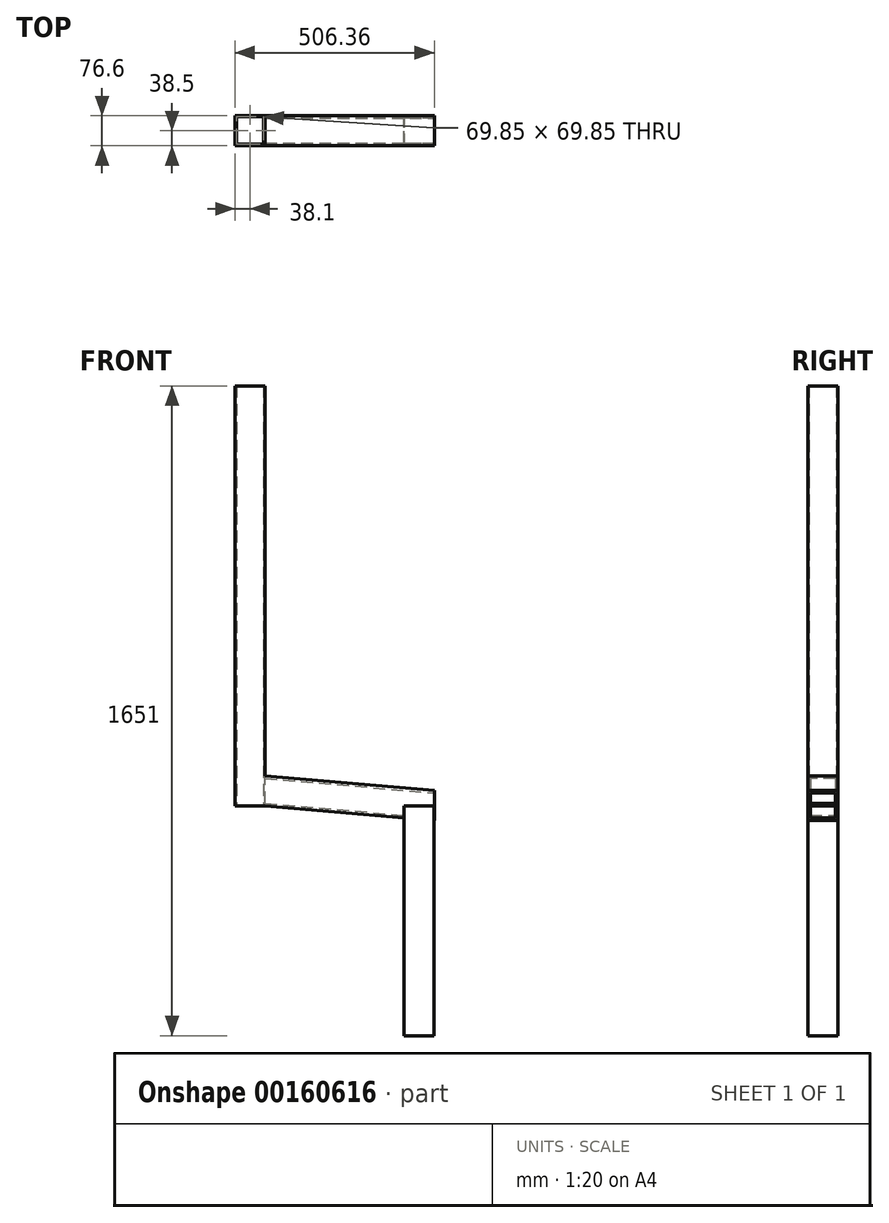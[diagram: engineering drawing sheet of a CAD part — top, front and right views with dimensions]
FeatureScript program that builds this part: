
annotation { "Feature Type Name" : "Feature", "Feature Type Description" : "" }
export const myFeature = defineFeature(function(context is Context, id is Id, definition is map)
    precondition{}
    {
        {
            var Q0;
            Q0=qCreatedBy(makeId("Top.planeOp"),FACE);
            var sketch = newSketch(context, id + "F0", { "sketchPlane" : qUnion([Q0])});
            skLineSegment(sketch, "E0.bottom", {"start": v(-38.1, -38.1) * mm, "end": v(38.1, -38.1) * mm});
            skLineSegment(sketch, "E0.top", {"start": v(-38.1, 38.1) * mm, "end": v(38.1, 38.1) * mm});
            skLineSegment(sketch, "E0.left", {"start": v(-38.1, -38.1) * mm, "end": v(-38.1, 38.1) * mm});
            skLineSegment(sketch, "E0.right", {"start": v(38.1, -38.1) * mm, "end": v(38.1, 38.1) * mm});
            skPoint(sketch, "E0.middle", {"position": v(0, 0) * mm});
            skLineSegment(sketch, "E1.bottom", {"start": v(-34.92, -38.22) * mm, "end": v(34.93, -38.22) * mm});
            skLineSegment(sketch, "E1.top", {"start": v(-34.93, 38.22) * mm, "end": v(34.92, 38.22) * mm});
            skLineSegment(sketch, "E1.left", {"start": v(-34.92, -38.22) * mm, "end": v(-34.93, 38.22) * mm});
            skLineSegment(sketch, "E1.right", {"start": v(34.93, -38.22) * mm, "end": v(34.92, 38.22) * mm});
            skSolve(sketch);
        }
        {
            var Q0;
            Q0=makeQuery(id+"F0.imprint","IMPRINT",FACE,{"disambiguationData":[TD([[makeQuery(id+"F0.imprint","IMPRINT",EDGE,{"derivedFrom":sQuery(id+"F0.wireOp",EDGE,"E0.bottom")}),1.0]])]});
            extrude(context, id + "F1", {"entities" : qUnion([Q0]), "depth" : 1066.8 * mm});
        }
        {
            var Q0;
            Q0=makeQuery(id+"F1.opExtrude","SWEPT_FACE",FACE,{"disambiguationData":[OSD([sQuery(id+"F0.wireOp",EDGE,"E0.right")])]});
            var sketch = newSketch(context, id + "F2", { "sketchPlane" : qUnion([Q0])});
            skLineSegment(sketch, "E2", {"start": v(0, 0) * mm, "end": v(0, 38.1) * mm});
            skLineSegment(sketch, "E3.bottom", {"start": v(38.1, 0) * mm, "end": v(-38.1, 0) * mm});
            skLineSegment(sketch, "E3.top", {"start": v(38.1, 76.2) * mm, "end": v(-38.1, 76.2) * mm});
            skLineSegment(sketch, "E3.left", {"start": v(38.1, 0) * mm, "end": v(38.1, 76.2) * mm});
            skLineSegment(sketch, "E3.right", {"start": v(-38.1, 0) * mm, "end": v(-38.1, 76.2) * mm});
            skPoint(sketch, "E3.middle", {"position": v(0, 38.1) * mm});
            skLineSegment(sketch, "E4.bottom", {"start": v(31.75, 6.35) * mm, "end": v(-31.75, 6.35) * mm});
            skLineSegment(sketch, "E4.top", {"start": v(31.75, 69.85) * mm, "end": v(-31.75, 69.85) * mm});
            skLineSegment(sketch, "E4.left", {"start": v(31.75, 6.35) * mm, "end": v(31.75, 69.85) * mm});
            skLineSegment(sketch, "E4.right", {"start": v(-31.75, 6.35) * mm, "end": v(-31.75, 69.85) * mm});
            skSolve(sketch);
        }
        {
            var Q0;
            Q0=qCreatedBy(makeId("Front.planeOp"),FACE);
            var sketch = newSketch(context, id + "F3", { "sketchPlane" : qUnion([Q0])});
            skLineSegment(sketch, "E5", {"start": v(38.27, 38.21) * mm, "end": v(468.42, 0.58) * mm});
            skSolve(sketch);
        }
        {
            var Q0;
            Q0=makeQuery(id+"F2.imprint","IMPRINT",FACE,{"disambiguationData":[TD([[makeQuery(id+"F2.imprint","IMPRINT",EDGE,{"derivedFrom":sQuery(id+"F2.wireOp",EDGE,"E3.top")}),1.0]])]});
            var Q1;
            Q1=sQuery(id+"F3.wireOp",EDGE,"E5");
            sweep(context, id + "F4", {"operationType" : NewBodyOperationType.ADD, "profiles" : qUnion([Q0]), "path" : qUnion([Q1])});
        }
        {
            var Q0;
            Q0=qCreatedBy(makeId("Top.planeOp"),FACE);
            var sketch = newSketch(context, id + "F5", { "sketchPlane" : qUnion([Q0])});
            skLineSegment(sketch, "E6.bottom", {"start": v(34.92, 34.93) * mm, "end": v(-34.93, 34.93) * mm});
            skLineSegment(sketch, "E6.top", {"start": v(34.93, -34.93) * mm, "end": v(-34.92, -34.93) * mm});
            skLineSegment(sketch, "E6.left", {"start": v(34.92, 34.93) * mm, "end": v(34.93, -34.93) * mm});
            skLineSegment(sketch, "E6.right", {"start": v(-34.93, 34.93) * mm, "end": v(-34.92, -34.93) * mm});
            skPoint(sketch, "E6.middle", {"position": v(0, 0) * mm});
            skSolve(sketch);
        }
        {
            var Q0;
            Q0 = qSketchRegion(id + "F5", true);
            extrude(context, id + "F6", {"entities" : qUnion([Q0]), "operationType" : NewBodyOperationType.REMOVE, "endBound" : BoundingType.THROUGH_ALL, "depth" : 25.4 * mm});
        }
        {
            var Q0;
            Q0=qCreatedBy(makeId("Top.planeOp"),FACE);
            var sketch = newSketch(context, id + "F7", { "sketchPlane" : qUnion([Q0])});
            skLineSegment(sketch, "E7.bottom", {"start": v(467.68, -38.5) * mm, "end": v(391.48, -38.5) * mm});
            skLineSegment(sketch, "E7.top", {"start": v(467.68, 38.1) * mm, "end": v(391.48, 38.1) * mm});
            skLineSegment(sketch, "E7.left", {"start": v(467.68, -38.5) * mm, "end": v(467.68, 38.1) * mm});
            skLineSegment(sketch, "E7.right", {"start": v(391.48, -38.5) * mm, "end": v(391.48, 38.1) * mm});
            skSolve(sketch);
        }
        {
            var Q0;
            Q0 = qSketchRegion(id + "F7", true);
            extrude(context, id + "F8", {"entities" : qUnion([Q0]), "operationType" : NewBodyOperationType.ADD, "oppositeDirection" : true, "depth" : 584.2 * mm});
        }
    });
